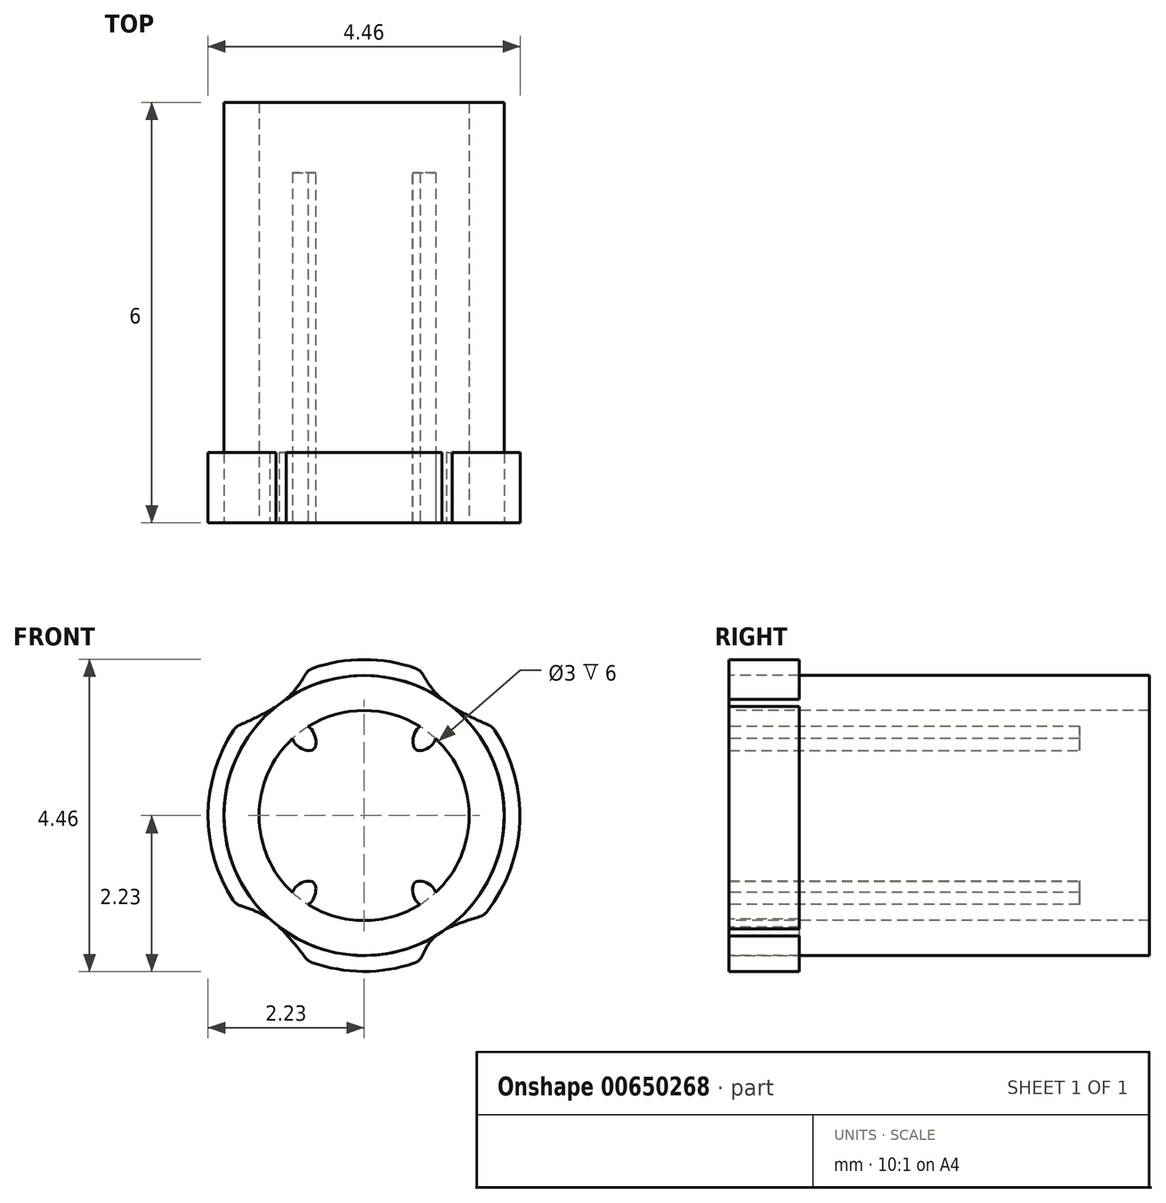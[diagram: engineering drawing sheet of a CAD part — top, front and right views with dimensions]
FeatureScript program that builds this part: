
annotation { "Feature Type Name" : "Feature", "Feature Type Description" : "" }
export const myFeature = defineFeature(function(context is Context, id is Id, definition is map)
    precondition{}
    {
        {
            var Q0;
            Q0=qCreatedBy(makeId("Front.planeOp"),FACE);
            var sketch = newSketch(context, id + "F0", { "sketchPlane" : qUnion([Q0])});
            skCircle(sketch, "E0", {"center": v(0, 0) * mm, "radius": 2 * mm});
            skSolve(sketch);
        }
        {
            var Q0;
            Q0 = qSketchRegion(id + "F0", true);
            extrude(context, id + "F1", {"entities" : qUnion([Q0]), "depth" : 6 * mm, "offsetDistance" : 25 * mm});
        }
        {
            var Q0;
            Q0=makeQuery(id+"F1.opExtrude","CAP_FACE",FACE,{"disambiguationData":[OSD([sQuery(id+"F0.wireOp",EDGE,"E0")])],"isStart":false});
            var sketch = newSketch(context, id + "F2", { "sketchPlane" : qUnion([Q0])});
            skCircle(sketch, "E1", {"center": v(0, 0) * mm, "radius": 1.5 * mm});
            skSolve(sketch);
        }
        {
            var Q0;
            Q0 = qSketchRegion(id + "F2", true);
            extrude(context, id + "F3", {"entities" : qUnion([Q0]), "operationType" : NewBodyOperationType.REMOVE, "endBound" : BoundingType.THROUGH_ALL, "oppositeDirection" : true, "depth" : 25 * mm, "offsetDistance" : 25 * mm});
        }
        {
            var Q0;
            Q0=makeQuery(id+"F1.opExtrude","CAP_FACE",FACE,{"disambiguationData":[OSD([sQuery(id+"F0.wireOp",EDGE,"E0")])],"isStart":false});
            var sketch = newSketch(context, id + "F4", { "sketchPlane" : qUnion([Q0])});
            skPoint(sketch, "E2", {"position": v(1.02, 1.1) * mm});
            skPoint(sketch, "E3", {"position": v(1.02, -1.1) * mm});
            skPoint(sketch, "E4", {"position": v(-1.02, -1.1) * mm});
            skFitSpline(sketch, "E5", {"points": [v(-0.8, 1.27) * mm, v(-1.02, 1.1) * mm, v(-0.73, 0.94) * mm, v(-0.8, 1.27) * mm]});
            skFitSpline(sketch, "E6", {"points": [v(-0.8, 1.27) * mm, v(-1.02, 1.1) * mm], "startDerivative": vector(-0.29, -0.24) * mm, "endDerivative": vector(-0.29, -0.24) * mm});
            skPoint(sketch, "E7.1.internal.orphan", {"position": v(0.8, 1.27) * mm});
            skFitSpline(sketch, "E8", {"points": [v(1.02, 1.1) * mm, v(0.8, 1.27) * mm, v(0.74, 0.94) * mm, v(1.02, 1.1) * mm]});
            skFitSpline(sketch, "E9", {"points": [v(1.02, 1.1) * mm, v(0.8, 1.27) * mm], "startDerivative": vector(-0.29, 0.24) * mm, "endDerivative": vector(-0.29, 0.24) * mm});
            skPoint(sketch, "E10", {"position": v(0.8, -1.27) * mm});
            skPoint(sketch, "E11", {"position": v(-0.8, -1.27) * mm});
            skFitSpline(sketch, "E12", {"points": [v(-1.02, -1.1) * mm, v(-0.8, -1.27) * mm, v(-0.73, -0.95) * mm, v(-1.02, -1.1) * mm]});
            skFitSpline(sketch, "E13", {"points": [v(-1.02, -1.1) * mm, v(-0.8, -1.27) * mm], "startDerivative": vector(0.22, -0.17) * mm, "endDerivative": vector(0.22, -0.17) * mm});
            skFitSpline(sketch, "E14", {"points": [v(1.02, -1.1) * mm, v(0.73, -0.95) * mm, v(0.8, -1.27) * mm, v(1.02, -1.1) * mm]});
            skFitSpline(sketch, "E15", {"points": [v(0.8, -1.27) * mm, v(1.02, -1.1) * mm], "startDerivative": vector(0.22, 0.17) * mm, "endDerivative": vector(0.22, 0.17) * mm});
            skSolve(sketch);
        }
        {
            var Q0;
            Q0 = qSketchRegion(id + "F4", true);
            extrude(context, id + "F5", {"entities" : qUnion([Q0]), "operationType" : NewBodyOperationType.ADD, "oppositeDirection" : true, "depth" : 5 * mm, "offsetDistance" : 25 * mm});
        }
        {
            var Q0;
            Q0=makeQuery(id+"F5.boolean.opBoolean","MERGE",FACE,{"derivedFrom":[makeQuery(id+"F1.opExtrude","CAP_FACE",FACE,{"disambiguationData":[OSD([sQuery(id+"F0.wireOp",EDGE,"E0")])],"isStart":false}),makeQuery(id+"F5.opExtrude","CAP_FACE",FACE,{"disambiguationData":[OSD([sQuery(id+"F4.wireOp",EDGE,"E5"),sQuery(id+"F4.wireOp",EDGE,"E6")])],"isStart":true}),makeQuery(id+"F5.opExtrude","CAP_FACE",FACE,{"disambiguationData":[OSD([sQuery(id+"F4.wireOp",EDGE,"E8"),sQuery(id+"F4.wireOp",EDGE,"E9")])],"isStart":true}),makeQuery(id+"F5.opExtrude","CAP_FACE",FACE,{"disambiguationData":[OSD([sQuery(id+"F4.wireOp",EDGE,"E12"),sQuery(id+"F4.wireOp",EDGE,"E13")])],"isStart":true}),makeQuery(id+"F5.opExtrude","CAP_FACE",FACE,{"disambiguationData":[OSD([sQuery(id+"F4.wireOp",EDGE,"E14"),sQuery(id+"F4.wireOp",EDGE,"E15")])],"isStart":true})]});
            var sketch = newSketch(context, id + "F6", { "sketchPlane" : qUnion([Q0])});
            skCircle(sketch, "E16", {"center": v(0, 0) * mm, "radius": 2.23 * mm});
            skFitSpline(sketch, "E17", {"points": [v(-0.8, 2.08) * mm, v(-1.11, 1.66) * mm, v(-1.83, 1.27) * mm], "startDerivative": vector(-0.57, -1) * mm, "endDerivative": vector(-1.45, -0.64) * mm});
            skPoint(sketch, "E18", {"position": v(-1.83, -1.27) * mm});
            skPoint(sketch, "E19", {"position": v(-0.8, -2.08) * mm});
            skPoint(sketch, "E20", {"position": v(1.83, 1.27) * mm});
            skPoint(sketch, "E21", {"position": v(0.8, 2.08) * mm});
            skPoint(sketch, "E22", {"position": v(0.8, -2.08) * mm});
            skPoint(sketch, "E23", {"position": v(1.7, -1.43) * mm});
            skPoint(sketch, "E24", {"position": v(-1.11, -1) * mm});
            skPoint(sketch, "E25", {"position": v(1.11, 1.66) * mm});
            skPoint(sketch, "E26", {"position": v(1.02, -1.72) * mm});
            skFitSpline(sketch, "E27", {"points": [v(0.8, 2.08) * mm, v(1.11, 1.66) * mm, v(1.83, 1.27) * mm], "startDerivative": vector(0.58, -0.99) * mm, "endDerivative": vector(1.45, -0.64) * mm});
            skFitSpline(sketch, "E28", {"points": [v(1.7, -1.43) * mm, v(1.02, -1.72) * mm, v(0.8, -2.08) * mm], "startDerivative": vector(-1.4, -0.42) * mm, "endDerivative": vector(-0.37, -0.9) * mm});
            skFitSpline(sketch, "E29", {"points": [v(-0.8, -2.08) * mm, v(-1.35, -1.48) * mm, v(-1.83, -1.27) * mm], "startDerivative": vector(-0.96, 1.25) * mm, "endDerivative": vector(-1.1, 0.33) * mm});
            skSolve(sketch);
        }
        {
            var Q0;
            {var subQ0=sQuery(id+"F6.wireOp",EDGE,"E17");var subQ1=sQuery(id+"F6.wireOp",EDGE,"E16");var subQ2=makeQuery(id+"F6.imprint","INTERSECT",VERTEX,{"disambiguationData":[OD(1.0)],"derivedFrom":[subQ1,subQ0]});Q0=makeQuery(id+"F6.imprint","IMPRINT",FACE,{"disambiguationData":[TD([[makeQuery(id+"F6.imprint","IMPRINT",EDGE,{"disambiguationData":[TD([[subQ2,-1.0]])],"derivedFrom":subQ1}),1.0]])]});}
            var Q1;
            {var subQ0=sQuery(id+"F6.wireOp",EDGE,"E17");var subQ1=sQuery(id+"F6.wireOp",EDGE,"E16");var subQ2=makeQuery(id+"F6.imprint","INTERSECT",VERTEX,{"disambiguationData":[OD(0.0)],"derivedFrom":[subQ1,subQ0]});Q1=makeQuery(id+"F6.imprint","IMPRINT",FACE,{"disambiguationData":[TD([[makeQuery(id+"F6.imprint","IMPRINT",EDGE,{"disambiguationData":[TD([[subQ2,1.0]])],"derivedFrom":subQ1}),1.0]])]});}
            var Q2;
            {var subQ0=sQuery(id+"F6.wireOp",EDGE,"E27");var subQ1=sQuery(id+"F6.wireOp",EDGE,"E16");var subQ2=makeQuery(id+"F6.imprint","INTERSECT",VERTEX,{"disambiguationData":[OD(1.0)],"derivedFrom":[subQ1,subQ0]});Q2=makeQuery(id+"F6.imprint","IMPRINT",FACE,{"disambiguationData":[TD([[makeQuery(id+"F6.imprint","IMPRINT",EDGE,{"disambiguationData":[TD([[subQ2,1.0]])],"derivedFrom":subQ1}),1.0]])]});}
            var Q3;
            {var subQ0=sQuery(id+"F6.wireOp",EDGE,"E28");var subQ1=sQuery(id+"F6.wireOp",EDGE,"E16");var subQ2=makeQuery(id+"F6.imprint","INTERSECT",VERTEX,{"disambiguationData":[OD(1.0)],"derivedFrom":[subQ1,subQ0]});Q3=makeQuery(id+"F6.imprint","IMPRINT",FACE,{"disambiguationData":[TD([[makeQuery(id+"F6.imprint","IMPRINT",EDGE,{"disambiguationData":[TD([[subQ2,1.0]])],"derivedFrom":subQ1}),1.0]])]});}
            extrude(context, id + "F7", {"entities" : qUnion([Q0, Q1, Q2, Q3]), "oppositeDirection" : true, "depth" : 1 * mm, "offsetDistance" : 25 * mm});
        }
        {
            var Q0;
            {var subQ0=sQuery(id+"F6.wireOp",EDGE,"E27");var subQ1=sQuery(id+"F6.wireOp",EDGE,"E16");Q0=makeQuery(id+"F7.opExtrude","SWEPT_EDGE",EDGE,{"disambiguationData":[OSD([subQ1,subQ0]),TDD([makeQuery(id+"F6.imprint","INTERSECT",VERTEX,{"disambiguationData":[OD(0.0)],"derivedFrom":[subQ1,subQ0]})])]});}
            var Q1;
            {var subQ0=sQuery(id+"F6.wireOp",EDGE,"E17");var subQ1=sQuery(id+"F6.wireOp",EDGE,"E16");Q1=makeQuery(id+"F7.opExtrude","SWEPT_EDGE",EDGE,{"disambiguationData":[OSD([subQ1,subQ0]),TDD([makeQuery(id+"F6.imprint","INTERSECT",VERTEX,{"disambiguationData":[OD(0.0)],"derivedFrom":[subQ1,subQ0]})])]});}
            var Q2;
            {var subQ0=sQuery(id+"F6.wireOp",EDGE,"E17");var subQ1=sQuery(id+"F6.wireOp",EDGE,"E16");Q2=makeQuery(id+"F7.opExtrude","SWEPT_EDGE",EDGE,{"disambiguationData":[OSD([subQ1,subQ0]),TDD([makeQuery(id+"F6.imprint","INTERSECT",VERTEX,{"disambiguationData":[OD(1.0)],"derivedFrom":[subQ1,subQ0]})])]});}
            var Q3;
            {var subQ0=sQuery(id+"F6.wireOp",EDGE,"E29");var subQ1=sQuery(id+"F6.wireOp",EDGE,"E16");Q3=makeQuery(id+"F7.opExtrude","SWEPT_EDGE",EDGE,{"disambiguationData":[OSD([subQ1,subQ0]),TDD([makeQuery(id+"F6.imprint","INTERSECT",VERTEX,{"disambiguationData":[OD(1.0)],"derivedFrom":[subQ1,subQ0]})])]});}
            var Q4;
            {var subQ0=sQuery(id+"F6.wireOp",EDGE,"E29");var subQ1=sQuery(id+"F6.wireOp",EDGE,"E16");Q4=makeQuery(id+"F7.opExtrude","SWEPT_EDGE",EDGE,{"disambiguationData":[OSD([subQ1,subQ0]),TDD([makeQuery(id+"F6.imprint","INTERSECT",VERTEX,{"disambiguationData":[OD(0.0)],"derivedFrom":[subQ1,subQ0]})])]});}
            var Q5;
            {var subQ0=sQuery(id+"F6.wireOp",EDGE,"E28");var subQ1=sQuery(id+"F6.wireOp",EDGE,"E16");Q5=makeQuery(id+"F7.opExtrude","SWEPT_EDGE",EDGE,{"disambiguationData":[OSD([subQ1,subQ0]),TDD([makeQuery(id+"F6.imprint","INTERSECT",VERTEX,{"disambiguationData":[OD(1.0)],"derivedFrom":[subQ1,subQ0]})])]});}
            var Q6;
            {var subQ0=sQuery(id+"F6.wireOp",EDGE,"E28");var subQ1=sQuery(id+"F6.wireOp",EDGE,"E16");Q6=makeQuery(id+"F7.opExtrude","SWEPT_EDGE",EDGE,{"disambiguationData":[OSD([subQ1,subQ0]),TDD([makeQuery(id+"F6.imprint","INTERSECT",VERTEX,{"disambiguationData":[OD(0.0)],"derivedFrom":[subQ1,subQ0]})])]});}
            var Q7;
            {var subQ0=sQuery(id+"F6.wireOp",EDGE,"E27");var subQ1=sQuery(id+"F6.wireOp",EDGE,"E16");Q7=makeQuery(id+"F7.opExtrude","SWEPT_EDGE",EDGE,{"disambiguationData":[OSD([subQ1,subQ0]),TDD([makeQuery(id+"F6.imprint","INTERSECT",VERTEX,{"disambiguationData":[OD(1.0)],"derivedFrom":[subQ1,subQ0]})])]});}
            fillet(context, id + "F8", {"entities" : qUnion([Q0, Q1, Q2, Q3, Q4, Q5, Q6, Q7]), "tangentPropagation" : true, "radius" : 0.2 * mm, "defaultsChanged" : true, "vertexSettings" : [], "allowEdgeOverflow" : false});
        }
    });
